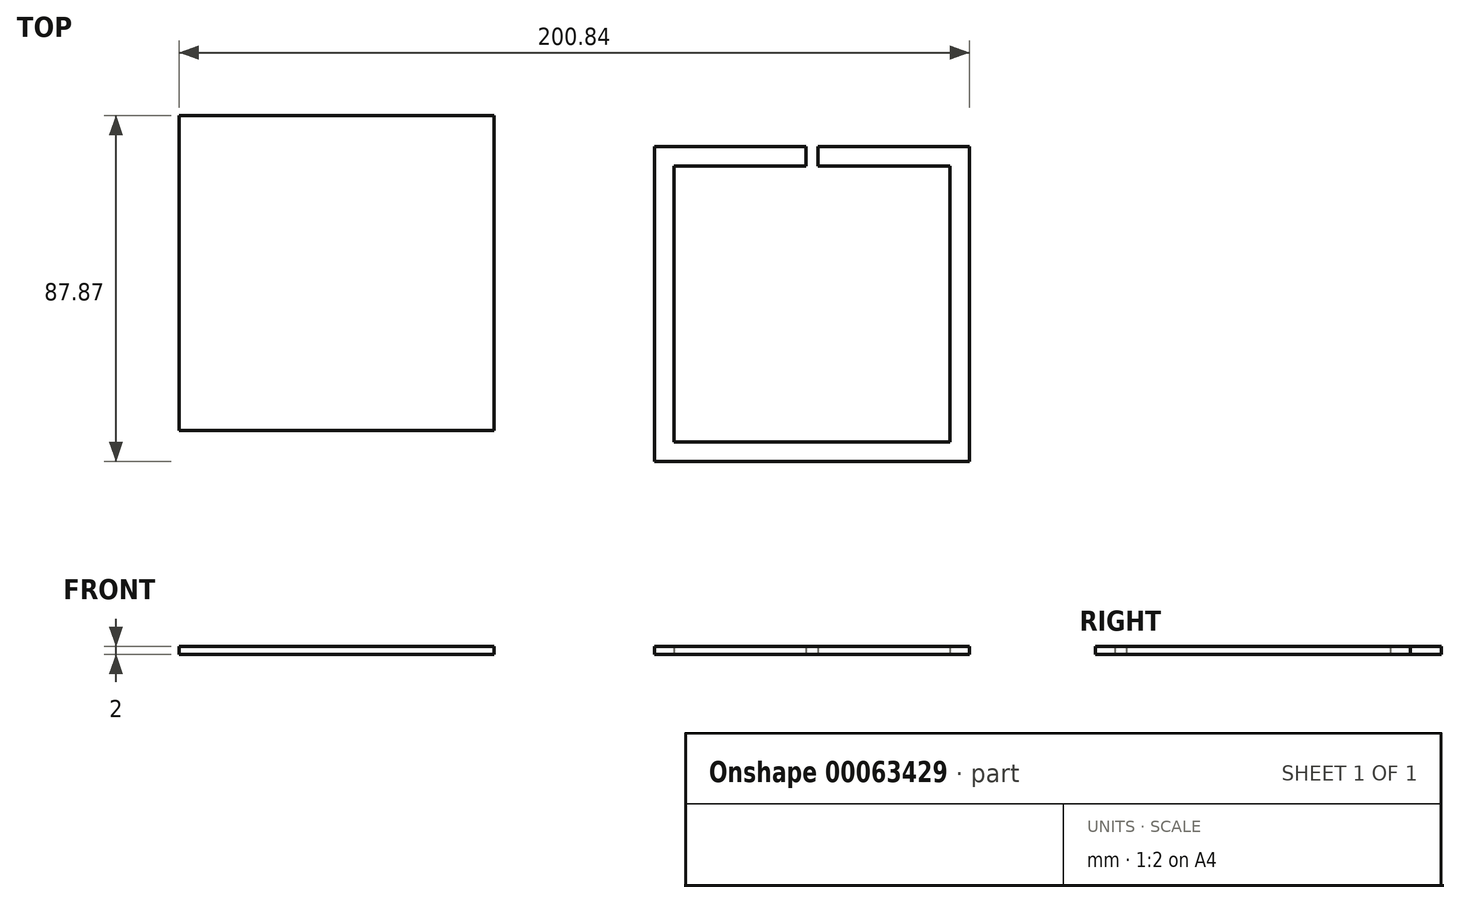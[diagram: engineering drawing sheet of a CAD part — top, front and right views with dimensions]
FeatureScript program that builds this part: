
annotation { "Feature Type Name" : "Feature", "Feature Type Description" : "" }
export const myFeature = defineFeature(function(context is Context, id is Id, definition is map)
    precondition{}
    {
        {
            var Q0;
            Q0=qCreatedBy(makeId("Top.planeOp"),FACE);
            var sketch = newSketch(context, id + "F0", { "sketchPlane" : qUnion([Q0])});
            skLineSegment(sketch, "E0.rect.bottom", {"start": v(25.4, -32.13) * mm, "end": v(-54.6, -32.13) * mm});
            skLineSegment(sketch, "E0.rect.top", {"start": v(25.4, 47.87) * mm, "end": v(-54.6, 47.87) * mm});
            skLineSegment(sketch, "E0.rect.left", {"start": v(25.4, -32.13) * mm, "end": v(25.4, 47.87) * mm});
            skLineSegment(sketch, "E0.rect.right", {"start": v(-54.6, -32.13) * mm, "end": v(-54.6, 47.87) * mm});
            skPoint(sketch, "E0.rect.middle", {"position": v(-14.6, 7.87) * mm});
            skSolve(sketch);
        }
        {
            var Q0;
            Q0=qCreatedBy(makeId("Top.planeOp"),FACE);
            var sketch = newSketch(context, id + "F1", { "sketchPlane" : qUnion([Q0])});
            skLineSegment(sketch, "E1.rect.bottom", {"start": v(146.24, -40) * mm, "end": v(66.24, -40) * mm});
            skLineSegment(sketch, "E1.rect.top", {"start": v(146.24, 40) * mm, "end": v(66.24, 40) * mm});
            skLineSegment(sketch, "E1.rect.left", {"start": v(146.24, -40) * mm, "end": v(146.24, 40) * mm});
            skLineSegment(sketch, "E1.rect.right", {"start": v(66.24, -40) * mm, "end": v(66.24, 40) * mm});
            skPoint(sketch, "E1.rect.middle", {"position": v(106.24, 0) * mm});
            skLineSegment(sketch, "E2.rect.bottom", {"start": v(141.24, -35) * mm, "end": v(71.24, -35) * mm});
            skLineSegment(sketch, "E2.rect.top", {"start": v(141.24, 35) * mm, "end": v(71.24, 35) * mm});
            skLineSegment(sketch, "E2.rect.left", {"start": v(141.24, -35) * mm, "end": v(141.24, 35) * mm});
            skLineSegment(sketch, "E2.rect.right", {"start": v(71.24, -35) * mm, "end": v(71.24, 35) * mm});
            skLineSegment(sketch, "E3", {"start": v(106.24, 40) * mm, "end": v(106.24, 0) * mm, "construction": true});
            skLineSegment(sketch, "E4", {"start": v(104.74, 40) * mm, "end": v(104.74, 35) * mm});
            skLineSegment(sketch, "E5.MirrorCS", {"start": v(107.74, 40) * mm, "end": v(107.74, 35) * mm});
            skSolve(sketch);
        }
        {
            var Q0;
            Q0=makeQuery(id+"F0.imprint","IMPRINT",FACE,{"disambiguationData":[TD([[makeQuery(id+"F0.imprint","IMPRINT",EDGE,{"derivedFrom":sQuery(id+"F0.wireOp",EDGE,"E0.rect.bottom")}),-1.0]])]});
            extrude(context, id + "F2", {"entities" : qUnion([Q0]), "depth" : 2 * mm});
        }
        {
            var Q0;
            Q0=makeQuery(id+"F1.imprint","IMPRINT",FACE,{"disambiguationData":[TD([[makeQuery(id+"F1.imprint","IMPRINT",EDGE,{"derivedFrom":sQuery(id+"F1.wireOp",EDGE,"E1.rect.bottom")}),-1.0]])]});
            extrude(context, id + "F3", {"entities" : qUnion([Q0]), "depth" : 2 * mm});
        }
    });
